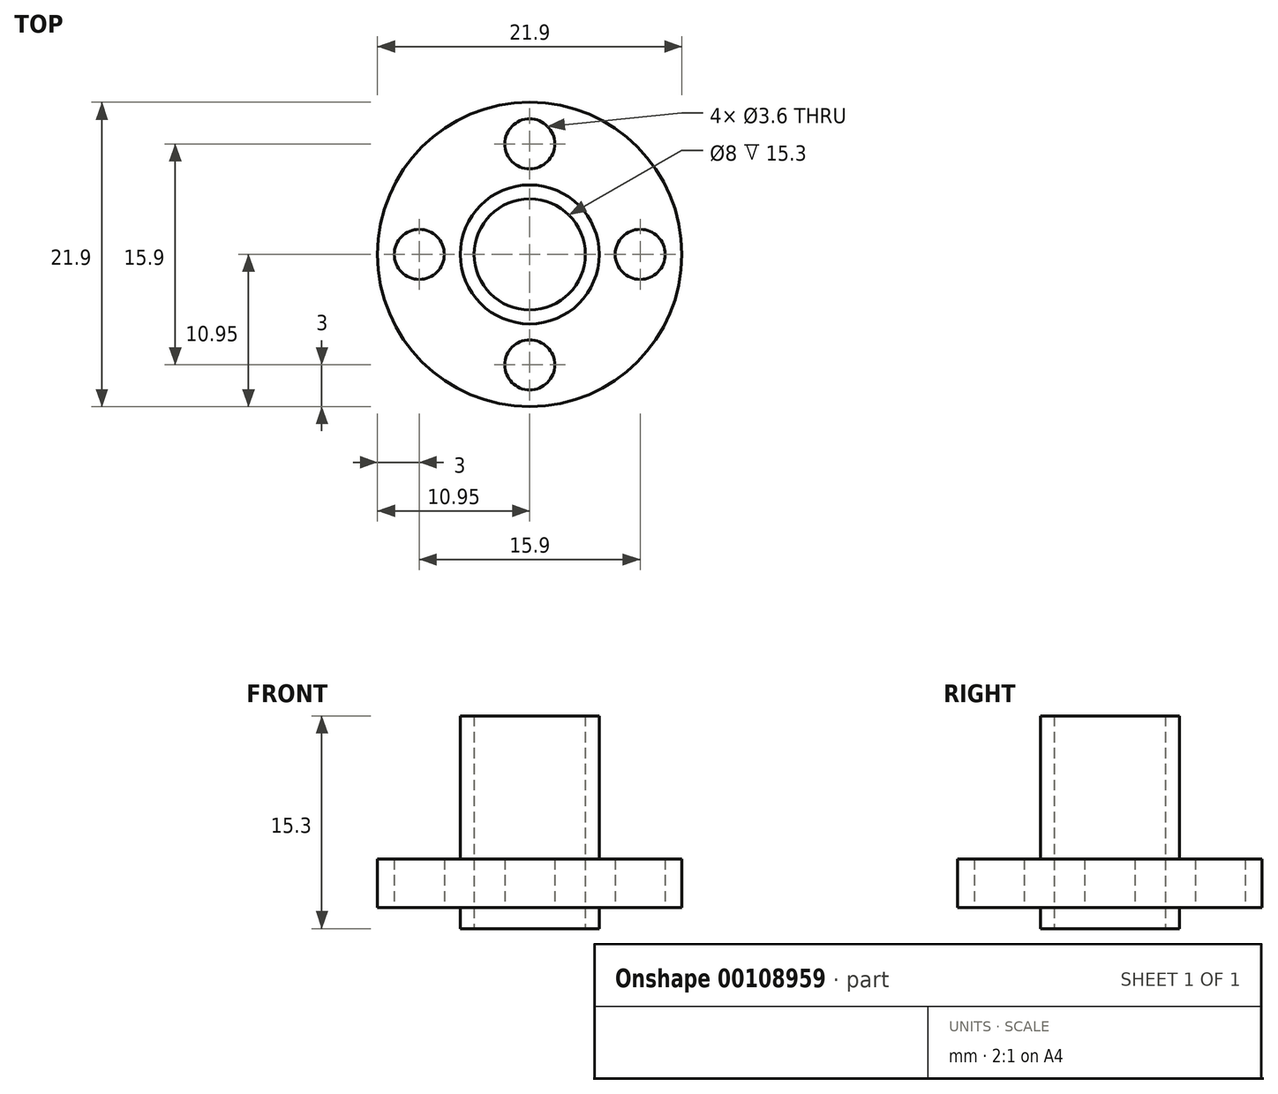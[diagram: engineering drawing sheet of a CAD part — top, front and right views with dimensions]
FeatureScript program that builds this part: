
annotation { "Feature Type Name" : "Feature", "Feature Type Description" : "" }
export const myFeature = defineFeature(function(context is Context, id is Id, definition is map)
    precondition{}
    {
        {
            var Q0;
            Q0=qCreatedBy(makeId("Top.planeOp"),FACE);
            var sketch = newSketch(context, id + "F0", { "sketchPlane" : qUnion([Q0])});
            skCircle(sketch, "E0", {"center": v(0, 0) * mm, "radius": 10.95 * mm});
            skCircle(sketch, "E1", {"center": v(0, 0) * mm, "radius": 4 * mm});
            skCircle(sketch, "E2", {"center": v(0, 0) * mm, "radius": 5 * mm});
            skCircle(sketch, "E3", {"center": v(-146.55, -52.44) * mm, "radius": 2.86 * mm});
            skCircle(sketch, "E4", {"center": v(0, 7.95) * mm, "radius": 1.8 * mm});
            skCircle(sketch, "E5.1.0", {"center": v(-7.95, 0) * mm, "radius": 1.8 * mm});
            skCircle(sketch, "E5.2.0", {"center": v(0, -7.95) * mm, "radius": 1.8 * mm});
            skCircle(sketch, "E5.3.0", {"center": v(7.95, 0) * mm, "radius": 1.8 * mm});
            skSolve(sketch);
        }
        {
            var Q0;
            Q0=makeQuery(id+"F0.imprint","IMPRINT",FACE,{"disambiguationData":[TD([[makeQuery(id+"F0.imprint","IMPRINT",EDGE,{"derivedFrom":sQuery(id+"F0.wireOp",EDGE,"E0")}),1.0]])]});
            extrude(context, id + "F1", {"entities" : qUnion([Q0]), "depth" : 3.5 * mm});
        }
        {
            var Q0;
            Q0=makeQuery(id+"F0.imprint","IMPRINT",FACE,{"disambiguationData":[TD([[makeQuery(id+"F0.imprint","IMPRINT",EDGE,{"derivedFrom":sQuery(id+"F0.wireOp",EDGE,"E1")}),-1.0]])]});
            extrude(context, id + "F2", {"entities" : qUnion([Q0]), "depth" : 13.8 * mm});
        }
        {
            var Q0;
            Q0=makeQuery(id+"F0.imprint","IMPRINT",FACE,{"disambiguationData":[TD([[makeQuery(id+"F0.imprint","IMPRINT",EDGE,{"derivedFrom":sQuery(id+"F0.wireOp",EDGE,"E1")}),-1.0]])]});
            extrude(context, id + "F3", {"entities" : qUnion([Q0]), "operationType" : NewBodyOperationType.ADD, "oppositeDirection" : true, "depth" : 1.5 * mm});
        }
    });
